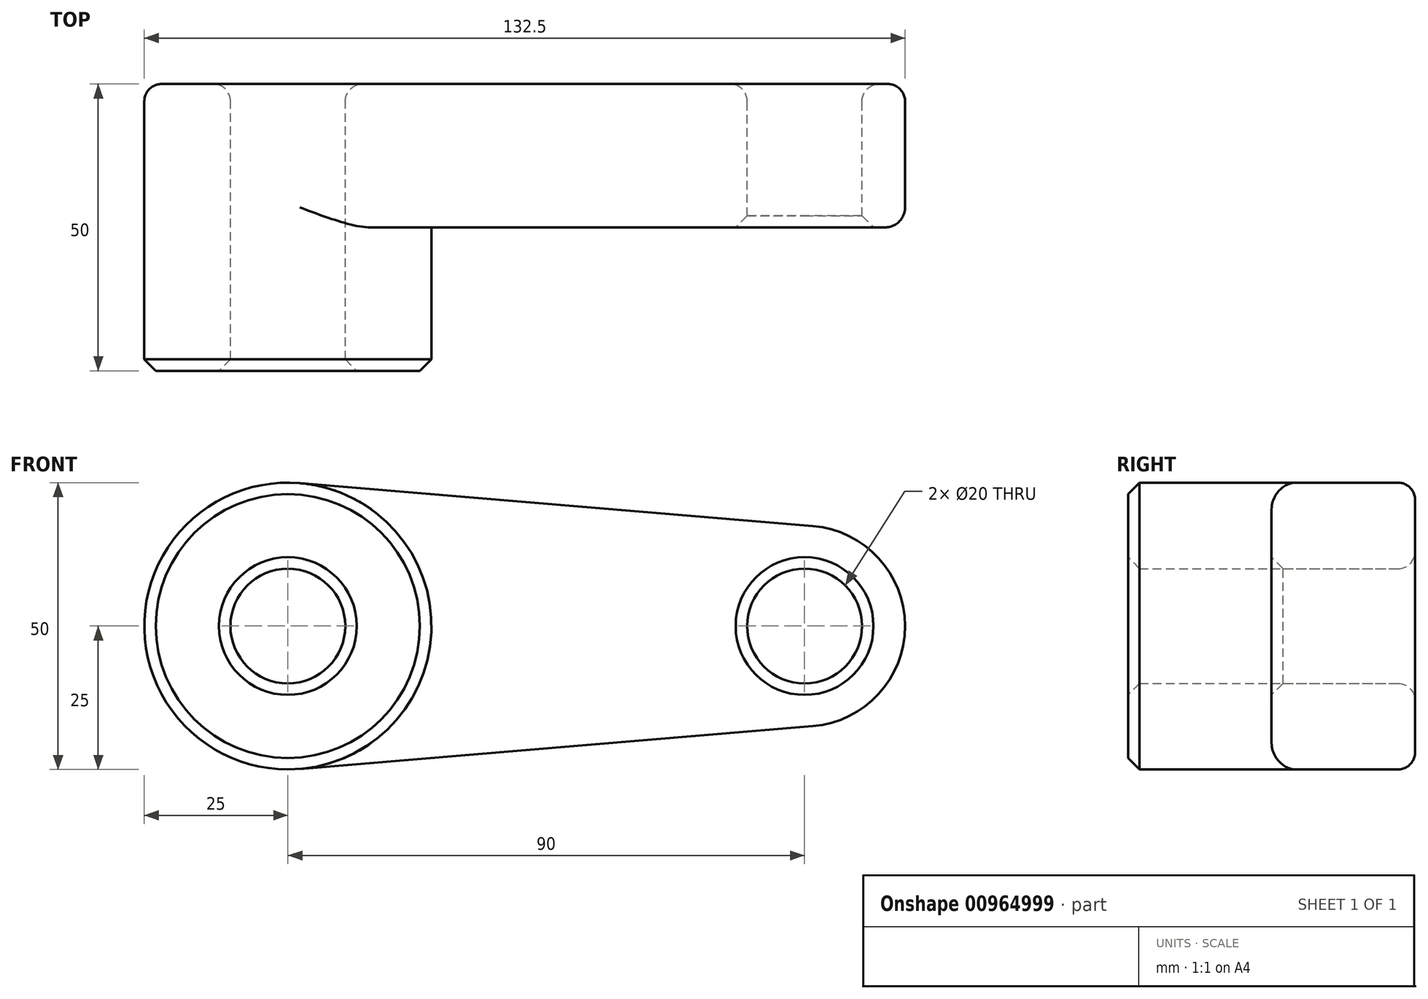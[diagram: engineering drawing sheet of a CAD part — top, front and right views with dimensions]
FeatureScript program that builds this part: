
annotation { "Feature Type Name" : "Feature", "Feature Type Description" : "" }
export const myFeature = defineFeature(function(context is Context, id is Id, definition is map)
    precondition{}
    {
        {
            var Q0;
            Q0=qCreatedBy(makeId("Front.planeOp"),FACE);
            var sketch = newSketch(context, id + "F0", { "sketchPlane" : qUnion([Q0])});
            skCircle(sketch, "E0", {"center": v(0, 0) * mm, "radius": 25 * mm});
            skCircle(sketch, "E1", {"center": v(90, 0) * mm, "radius": 17.5 * mm});
            skLineSegment(sketch, "E2", {"start": v(2.08, 24.91) * mm, "end": v(91.46, 17.44) * mm});
            skLineSegment(sketch, "E3", {"start": v(2.08, -24.91) * mm, "end": v(91.46, -17.44) * mm});
            skCircle(sketch, "E4", {"center": v(0, 0) * mm, "radius": 10 * mm});
            skCircle(sketch, "E5", {"center": v(90, 0) * mm, "radius": 10 * mm});
            skSolve(sketch);
        }
        {
            var Q0;
            Q0=makeQuery(id+"F0.imprint","IMPRINT",FACE,{"disambiguationData":[TD([[makeQuery(id+"F0.imprint","IMPRINT",EDGE,{"derivedFrom":sQuery(id+"F0.wireOp",EDGE,"E5")}),-1.0]])]});
            var Q1;
            {var subQ0=sQuery(id+"F0.wireOp",EDGE,"E2");Q1=makeQuery(id+"F0.imprint","IMPRINT",FACE,{"disambiguationData":[TD([[makeQuery(id+"F0.imprint","IMPRINT",EDGE,{"derivedFrom":subQ0}),-1.0]])]});}
            var Q2;
            Q2=makeQuery(id+"F0.imprint","IMPRINT",FACE,{"disambiguationData":[TD([[makeQuery(id+"F0.imprint","IMPRINT",EDGE,{"derivedFrom":sQuery(id+"F0.wireOp",EDGE,"E4")}),-1.0]])]});
            extrude(context, id + "F1", {"entities" : qUnion([Q0, Q1, Q2]), "depth" : 25 * mm, "offsetDistance" : 25 * mm});
        }
        {
            var Q0;
            Q0=makeQuery(id+"F0.imprint","IMPRINT",FACE,{"disambiguationData":[TD([[makeQuery(id+"F0.imprint","IMPRINT",EDGE,{"derivedFrom":sQuery(id+"F0.wireOp",EDGE,"E4")}),-1.0]])]});
            extrude(context, id + "F2", {"entities" : qUnion([Q0]), "operationType" : NewBodyOperationType.ADD, "depth" : 25 * mm, "offsetDistance" : 25 * mm});
        }
        {
            var Q0;
            Q0=makeQuery(id+"F0.imprint","IMPRINT",FACE,{"disambiguationData":[TD([[makeQuery(id+"F0.imprint","IMPRINT",EDGE,{"derivedFrom":sQuery(id+"F0.wireOp",EDGE,"E4")}),-1.0]])]});
            extrude(context, id + "F3", {"entities" : qUnion([Q0]), "operationType" : NewBodyOperationType.ADD, "depth" : 50 * mm, "offsetDistance" : 25 * mm});
        }
        {
            var Q0;
            Q0=makeQuery(id+"F3.opExtrude","CAP_EDGE",EDGE,{"disambiguationData":[OSD([sQuery(id+"F0.wireOp",EDGE,"E4")])],"isStart":false});
            var Q1;
            Q1=makeQuery(id+"F3.opExtrude","CAP_EDGE",EDGE,{"disambiguationData":[OSD([sQuery(id+"F0.wireOp",EDGE,"E0")])],"isStart":false});
            var Q2;
            Q2=makeQuery(id+"F1.opExtrude","CAP_EDGE",EDGE,{"disambiguationData":[OSD([sQuery(id+"F0.wireOp",EDGE,"E5")])],"isStart":false});
            chamfer(context, id + "F4", {"entities" : qUnion([Q0, Q1, Q2]), "width" : 2 * mm, "tangentPropagation" : true});
        }
        {
            var Q0;
            Q0=makeQuery(id+"F1.opExtrude","CAP_EDGE",EDGE,{"disambiguationData":[OSD([sQuery(id+"F0.wireOp",EDGE,"E3")])],"isStart":false});
            var Q1;
            Q1=makeQuery(id+"F1.opExtrude","CAP_EDGE",EDGE,{"disambiguationData":[OSD([sQuery(id+"F0.wireOp",EDGE,"E1")])],"isStart":false});
            var Q2;
            Q2=makeQuery(id+"F1.opExtrude","CAP_EDGE",EDGE,{"disambiguationData":[OSD([sQuery(id+"F0.wireOp",EDGE,"E2")])],"isStart":false});
            fillet(context, id + "F5", {"entities" : qUnion([Q0, Q1, Q2]), "radius" : 3.5 * mm, "tangentPropagation" : true, "allowEdgeOverflow" : false});
        }
        {
            var Q0;
            Q0=makeQuery(id+"F1.opExtrude","CAP_EDGE",EDGE,{"disambiguationData":[OSD([sQuery(id+"F0.wireOp",EDGE,"E4")])],"isStart":true});
            var Q1;
            Q1=makeQuery(id+"F1.opExtrude","CAP_EDGE",EDGE,{"disambiguationData":[OSD([sQuery(id+"F0.wireOp",EDGE,"E5")])],"isStart":true});
            var Q2;
            Q2=makeQuery(id+"F1.opExtrude","CAP_EDGE",EDGE,{"disambiguationData":[OSD([sQuery(id+"F0.wireOp",EDGE,"E1")])],"isStart":true});
            var Q3;
            Q3=makeQuery(id+"F1.opExtrude","CAP_EDGE",EDGE,{"disambiguationData":[OSD([sQuery(id+"F0.wireOp",EDGE,"E2")])],"isStart":true});
            var Q4;
            Q4=makeQuery(id+"F1.opExtrude","CAP_EDGE",EDGE,{"disambiguationData":[OSD([sQuery(id+"F0.wireOp",EDGE,"E0")])],"isStart":true});
            var Q5;
            Q5=makeQuery(id+"F1.opExtrude","CAP_EDGE",EDGE,{"disambiguationData":[OSD([sQuery(id+"F0.wireOp",EDGE,"E3")])],"isStart":true});
            fillet(context, id + "F6", {"entities" : qUnion([Q0, Q1, Q2, Q3, Q4, Q5]), "radius" : 3 * mm, "tangentPropagation" : true, "allowEdgeOverflow" : false});
        }
    });
